# Revit family: WWF-Welded Wide Flange
name_source: partatom
category: Structural Framing
revit_build: Autodesk Revit Architecture 2012 (Build: 20110210_1515)
units: mm (PartAtom-declared; Revit-internal decimal feet)

## types (107) — shared parameters
Assembly Code = B10
Nominal d = 12

## per-type parameters (varying)
| type | A | W | bf | d | k | tf | tw |
| WWF79x490 | 144 in² | 490 | 1' - 9 5/8" | 6' - 6 3/4" | 0' - 0 13/16" | 0' - 2" | 0' - 0 13/16" |
| WWF79x436 | 128 in² | 436 | 1' - 9 5/8" | 6' - 6 3/4" | 0' - 0 13/16" | 0' - 1 9/16" | 0' - 0 13/16" |
| WWF79x408 | 120 in² | 408 | 1' - 9 5/8" | 6' - 6 3/4" | 0' - 0 13/16" | 0' - 1 3/8" | 0' - 0 13/16" |
| WWF79x364 | 107 in² | 364 | 1' - 7 11/16" | 6' - 6 3/4" | 0' - 0 13/16" | 0' - 1 3/16" | 0' - 0 13/16" |
| WWF71x470 | 138 in² | 470 | 1' - 9 5/8" | 5' - 10 7/8" | 0' - 0 13/16" | 0' - 2" | 0' - 0 13/16" |
| WWF71x442 | 130 in² | 442 | 1' - 9 5/8" | 5' - 10 7/8" | 0' - 0 13/16" | 0' - 1 3/4" | 0' - 0 13/16" |
| WWF71x415 | 122 in² | 415 | 1' - 9 5/8" | 5' - 10 7/8" | 0' - 0 13/16" | 0' - 1 9/16" | 0' - 0 13/16" |
| WWF71x388 | 114 in² | 388 | 1' - 9 5/8" | 5' - 10 7/8" | 0' - 0 13/16" | 0' - 1 3/8" | 0' - 0 13/16" |
| WWF71x344 | 101 in² | 344 | 1' - 7 11/16" | 5' - 10 7/8" | 0' - 0 13/16" | 0' - 1 3/16" | 0' - 0 13/16" |
| WWF63x419 | 123 in² | 419 | 1' - 9 5/8" | 5' - 3" | 0' - 0 3/4" | 0' - 2" | 0' - 0 5/8" |
| WWF63x388 | 114 in² | 388 | 1' - 9 5/8" | 5' - 3" | 0' - 0 3/4" | 0' - 1 3/4" | 0' - 0 5/8" |
| WWF63x361 | 106 in² | 361 | 1' - 9 5/8" | 5' - 3" | 0' - 0 3/4" | 0' - 1 9/16" | 0' - 0 5/8" |
| WWF63x333 | 97.8 in² | 333 | 1' - 9 5/8" | 5' - 3" | 0' - 0 11/16" | 0' - 1 3/8" | 0' - 0 5/8" |
| WWF63x289 | 84.9 in² | 289 | 1' - 7 11/16" | 5' - 3" | 0' - 0 11/16" | 0' - 1 3/16" | 0' - 0 5/8" |
| WWF55x402 | 118 in² | 402 | 1' - 9 5/8" | 4' - 7 1/8" | 0' - 0 3/4" | 0' - 2" | 0' - 0 5/8" |
| WWF55x344 | 101 in² | 344 | 1' - 9 5/8" | 4' - 7 1/8" | 0' - 0 3/4" | 0' - 1 9/16" | 0' - 0 5/8" |
| WWF55x316 | 92.9 in² | 316 | 1' - 9 5/8" | 4' - 7 1/8" | 0' - 0 11/16" | 0' - 1 3/8" | 0' - 0 5/8" |
| WWF55x272 | 79.9 in² | 272 | 1' - 7 11/16" | 4' - 7 1/8" | 0' - 0 11/16" | 0' - 1 3/16" | 0' - 0 5/8" |
| WWF55x240 | 70.6 in² | 240 | 1' - 3 3/4" | 4' - 7 1/8" | 0' - 0 11/16" | 0' - 1 3/16" | 0' - 0 5/8" |
| WWF47x326 | 96.3 in² | 326 | 1' - 9 5/8" | 3' - 11 1/4" | 0' - 0 3/4" | 0' - 1 9/16" | 0' - 0 5/8" |
| WWF47x281 | 82.5 in² | 281 | 1' - 7 11/16" | 3' - 11 1/4" | 0' - 0 11/16" | 0' - 1 3/8" | 0' - 0 5/8" |
| WWF47x255 | 75 in² | 255 | 1' - 7 11/16" | 3' - 11 1/4" | 0' - 0 11/16" | 0' - 1 3/16" | 0' - 0 5/8" |
| WWF47x224 | 65.7 in² | 224 | 1' - 3 3/4" | 3' - 11 1/4" | 0' - 0 11/16" | 0' - 1 3/16" | 0' - 0 5/8" |
| WWF47x203 | 59.7 in² | 203 | 1' - 3 3/4" | 3' - 11 1/4" | 0' - 0 11/16" | 0' - 1" | 0' - 0 5/8" |
| WWF47x176 | 52 in² | 176 | 0' - 11 13/16" | 3' - 11 1/4" | 0' - 0 11/16" | 0' - 1" | 0' - 0 5/8" |
| WWF43x307 | 90.6 in² | 307 | 1' - 9 5/8" | 3' - 7 5/16" | 0' - 0 11/16" | 0' - 1 9/16" | 0' - 0 9/16" |
| WWF43x260 | 76.8 in² | 260 | 1' - 7 11/16" | 3' - 7 5/16" | 0' - 0 5/8" | 0' - 1 3/8" | 0' - 0 9/16" |
| WWF43x236 | 69.3 in² | 236 | 1' - 7 11/16" | 3' - 7 5/16" | 0' - 0 5/8" | 0' - 1 3/16" | 0' - 0 9/16" |
| WWF43x204 | 60 in² | 204 | 1' - 3 3/4" | 3' - 7 5/16" | 0' - 0 5/8" | 0' - 1 3/16" | 0' - 0 9/16" |
| WWF43x184 | 54 in² | 184 | 1' - 3 3/4" | 3' - 7 5/16" | 0' - 0 5/8" | 0' - 1" | 0' - 0 9/16" |
| WWF43x157 | 46.2 in² | 157 | 0' - 11 13/16" | 3' - 7 5/16" | 0' - 0 5/8" | 0' - 1" | 0' - 0 9/16" |
| WWF39x300 | 88.4 in² | 300 | 1' - 9 5/8" | 3' - 3 3/8" | 0' - 0 11/16" | 0' - 1 9/16" | 0' - 0 9/16" |
| WWF39x253 | 74.6 in² | 253 | 1' - 7 11/16" | 3' - 3 3/8" | 0' - 0 5/8" | 0' - 1 3/8" | 0' - 0 9/16" |
| WWF39x228 | 67.1 in² | 228 | 1' - 7 11/16" | 3' - 3 3/8" | 0' - 0 5/8" | 0' - 1 3/16" | 0' - 0 9/16" |
| WWF39x197 | 57.8 in² | 197 | 1' - 3 3/4" | 3' - 3 3/8" | 0' - 0 5/8" | 0' - 1 3/16" | 0' - 0 9/16" |
| WWF39x176 | 51.8 in² | 176 | 1' - 3 3/4" | 3' - 3 3/8" | 0' - 0 5/8" | 0' - 1" | 0' - 0 9/16" |
| WWF39x150 | 44.1 in² | 150 | 0' - 11 13/16" | 3' - 3 3/8" | 0' - 0 5/8" | 0' - 1" | 0' - 0 9/16" |
| WWF39x134 | 39.6 in² | 134 | 0' - 11 13/16" | 3' - 3 3/8" | 0' - 0 5/8" | 0' - 0 13/16" | 0' - 0 9/16" |
| WWF35x279 | 82.5 in² | 279 | 1' - 9 5/8" | 2' - 11 7/16" | 0' - 0 5/8" | 0' - 1 9/16" | 0' - 0 7/16" |
| WWF35x233 | 68.6 in² | 233 | 1' - 7 11/16" | 2' - 11 7/16" | 0' - 0 9/16" | 0' - 1 3/8" | 0' - 0 7/16" |
| WWF35x208 | 61 in² | 208 | 1' - 7 11/16" | 2' - 11 7/16" | 0' - 0 9/16" | 0' - 1 3/16" | 0' - 0 7/16" |
| WWF35x176 | 51.7 in² | 176 | 1' - 3 3/4" | 2' - 11 7/16" | 0' - 0 9/16" | 0' - 1 3/16" | 0' - 0 7/16" |
| WWF35x156 | 45.7 in² | 156 | 1' - 3 3/4" | 2' - 11 7/16" | 0' - 0 9/16" | 0' - 1" | 0' - 0 7/16" |
| WWF35x128 | 37.9 in² | 128 | 0' - 11 13/16" | 2' - 11 7/16" | 0' - 0 9/16" | 0' - 1" | 0' - 0 7/16" |
| WWF35x113 | 33.5 in² | 113 | 0' - 11 13/16" | 2' - 11 7/16" | 0' - 0 9/16" | 0' - 0 13/16" | 0' - 0 7/16" |
| WWF31x228 | 66.9 in² | 228 | 1' - 7 11/16" | 2' - 7 1/2" | 0' - 0 9/16" | 0' - 1 3/8" | 0' - 0 7/16" |
| WWF31x202 | 59.3 in² | 202 | 1' - 7 11/16" | 2' - 7 1/2" | 0' - 0 9/16" | 0' - 1 3/16" | 0' - 0 7/16" |
| WWF31x170 | 50 in² | 170 | 1' - 3 3/4" | 2' - 7 1/2" | 0' - 0 9/16" | 0' - 1 3/16" | 0' - 0 7/16" |
| WWF31x150 | 44 in² | 150 | 1' - 3 3/4" | 2' - 7 1/2" | 0' - 0 9/16" | 0' - 1" | 0' - 0 7/16" |
| WWF31x123 | 36.2 in² | 123 | 0' - 11 13/16" | 2' - 7 1/2" | 0' - 0 9/16" | 0' - 1" | 0' - 0 7/16" |
| WWF31x108 | 31.8 in² | 108 | 0' - 11 13/16" | 2' - 7 1/2" | 0' - 0 9/16" | 0' - 0 13/16" | 0' - 0 7/16" |
| WWF28x164 | 48.3 in² | 164 | 1' - 3 3/4" | 2' - 3 9/16" | 0' - 0 9/16" | 0' - 1 3/16" | 0' - 0 7/16" |
| WWF28x144 | 42.3 in² | 144 | 1' - 3 3/4" | 2' - 3 9/16" | 0' - 0 9/16" | 0' - 1" | 0' - 0 7/16" |
| WWF28x132 | 38.7 in² | 132 | 1' - 3 3/4" | 2' - 3 9/16" | 0' - 0 9/16" | 0' - 0 7/8" | 0' - 0 7/16" |
| WWF28x117 | 34.5 in² | 117 | 0' - 11 13/16" | 2' - 3 9/16" | 0' - 0 9/16" | 0' - 1" | 0' - 0 7/16" |
| WWF28x102 | 30 in² | 102 | 0' - 11 13/16" | 2' - 3 9/16" | 0' - 0 9/16" | 0' - 0 13/16" | 0' - 0 7/16" |
| WWF26x580 | 170 in² | 580 | 2' - 1 9/16" | 2' - 1 9/16" | 0' - 1 5/8" | 0' - 2 3/8" | 0' - 2 3/8" |
| WWF26x497 | 146 in² | 497 | 2' - 1 9/16" | 2' - 1 9/16" | 0' - 1" | 0' - 2 3/8" | 0' - 1 3/16" |
| WWF26x402 | 118 in² | 402 | 2' - 1 9/16" | 2' - 1 9/16" | 0' - 0 13/16" | 0' - 2" | 0' - 0 13/16" |
| WWF26x336 | 98.5 in² | 336 | 2' - 1 9/16" | 2' - 1 9/16" | 0' - 0 13/16" | 0' - 1 9/16" | 0' - 0 13/16" |
| WWF26x269 | 79 in² | 269 | 2' - 1 9/16" | 2' - 1 9/16" | 0' - 0 13/16" | 0' - 1 3/16" | 0' - 0 13/16" |
| WWF24x531 | 157 in² | 531 | 1' - 11 5/8" | 1' - 11 5/8" | 0' - 1 5/8" | 0' - 2 3/8" | 0' - 2 3/8" |
| WWF24x456 | 134 in² | 456 | 1' - 11 5/8" | 1' - 11 5/8" | 0' - 1" | 0' - 2 3/8" | 0' - 1 3/16" |
| WWF24x371 | 109 in² | 371 | 1' - 11 5/8" | 1' - 11 5/8" | 0' - 0 13/16" | 0' - 2" | 0' - 0 13/16" |
| WWF24x309 | 90.8 in² | 309 | 1' - 11 5/8" | 1' - 11 5/8" | 0' - 0 13/16" | 0' - 1 9/16" | 0' - 0 13/16" |
| WWF24x248 | 72.8 in² | 248 | 1' - 11 5/8" | 1' - 11 5/8" | 0' - 0 13/16" | 0' - 1 3/16" | 0' - 0 13/16" |
| WWF22x484 | 143 in² | 484 | 1' - 9 5/8" | 1' - 9 5/8" | 0' - 1 7/8" | 0' - 2 3/8" | 0' - 2 3/8" |
| WWF22x416 | 123 in² | 416 | 1' - 9 5/8" | 1' - 9 5/8" | 0' - 1" | 0' - 2 3/8" | 0' - 1 3/16" |
| WWF22x338 | 99.5 in² | 338 | 1' - 9 5/8" | 1' - 9 5/8" | 0' - 0 13/16" | 0' - 2" | 0' - 0 13/16" |
| WWF22x282 | 83 in² | 282 | 1' - 9 5/8" | 1' - 9 5/8" | 0' - 0 13/16" | 0' - 1 9/16" | 0' - 0 13/16" |
| WWF22x188 | 55.2 in² | 188 | 1' - 9 5/8" | 1' - 9 5/8" | 0' - 0 11/16" | 0' - 1" | 0' - 0 5/8" |
| WWF20x437 | 129 in² | 437 | 1' - 7 11/16" | 1' - 7 11/16" | 0' - 1 7/8" | 0' - 2 3/8" | 0' - 2 3/8" |
| WWF20x377 | 111 in² | 377 | 1' - 7 11/16" | 1' - 7 11/16" | 0' - 1" | 0' - 2 3/8" | 0' - 1 3/16" |
| WWF20x306 | 90.2 in² | 306 | 1' - 7 11/16" | 1' - 7 11/16" | 0' - 0 13/16" | 0' - 2" | 0' - 0 13/16" |
| WWF20x256 | 75.3 in² | 256 | 1' - 7 11/16" | 1' - 7 11/16" | 0' - 0 13/16" | 0' - 1 9/16" | 0' - 0 13/16" |
| WWF20x230 | 67.9 in² | 230 | 1' - 7 11/16" | 1' - 7 11/16" | 0' - 0 13/16" | 0' - 1 3/8" | 0' - 0 13/16" |
| WWF20x205 | 60.4 in² | 205 | 1' - 7 11/16" | 1' - 7 11/16" | 0' - 0 13/16" | 0' - 1 3/16" | 0' - 0 13/16" |
| WWF20x185 | 54.6 in² | 185 | 1' - 7 11/16" | 1' - 7 11/16" | 0' - 0 13/16" | 0' - 1 1/8" | 0' - 0 5/8" |
| WWF20x170 | 50.1 in² | 170 | 1' - 7 11/16" | 1' - 7 11/16" | 0' - 0 13/16" | 0' - 1" | 0' - 0 5/8" |
| WWF20x150 | 44.2 in² | 150 | 1' - 7 11/16" | 1' - 7 11/16" | 0' - 0 5/8" | 0' - 0 7/8" | 0' - 0 9/16" |
| WWF20x132 | 39 in² | 132 | 1' - 7 11/16" | 1' - 7 11/16" | 0' - 0 9/16" | 0' - 0 13/16" | 0' - 0 7/16" |
| WWF18x337 | 99.3 in² | 337 | 1' - 5 3/4" | 1' - 5 3/4" | 0' - 1" | 0' - 2 3/8" | 0' - 1 3/16" |
| WWF18x275 | 80.9 in² | 275 | 1' - 5 3/4" | 1' - 5 3/4" | 0' - 0 13/16" | 0' - 2" | 0' - 0 13/16" |
| WWF18x229 | 67.5 in² | 229 | 1' - 5 3/4" | 1' - 5 3/4" | 0' - 0 13/16" | 0' - 1 9/16" | 0' - 0 13/16" |
| WWF18x207 | 60.9 in² | 207 | 1' - 5 3/4" | 1' - 5 3/4" | 0' - 0 13/16" | 0' - 1 3/8" | 0' - 0 13/16" |
| WWF18x184 | 54.2 in² | 184 | 1' - 5 3/4" | 1' - 5 3/4" | 0' - 0 13/16" | 0' - 1 3/16" | 0' - 0 13/16" |
| WWF18x166 | 49 in² | 166 | 1' - 5 3/4" | 1' - 5 3/4" | 0' - 0 11/16" | 0' - 1 1/8" | 0' - 0 5/8" |
| WWF18x152 | 45 in² | 152 | 1' - 5 3/4" | 1' - 5 3/4" | 0' - 0 11/16" | 0' - 1" | 0' - 0 5/8" |
| WWF18x134 | 39.7 in² | 134 | 1' - 5 3/4" | 1' - 5 3/4" | 0' - 0 5/8" | 0' - 0 7/8" | 0' - 0 9/16" |
| WWF18x119 | 35.1 in² | 119 | 1' - 5 3/4" | 1' - 5 3/4" | 0' - 0 9/16" | 0' - 0 13/16" | 0' - 0 7/16" |
| WWF16x298 | 87.7 in² | 298 | 1' - 3 3/4" | 1' - 3 3/4" | 0' - 1" | 0' - 2 3/8" | 0' - 1 3/16" |
| WWF16x243 | 71.6 in² | 243 | 1' - 3 3/4" | 1' - 3 3/4" | 0' - 0 13/16" | 0' - 2" | 0' - 0 13/16" |
| WWF16x203 | 59.8 in² | 203 | 1' - 3 3/4" | 1' - 3 3/4" | 0' - 0 13/16" | 0' - 1 9/16" | 0' - 0 13/16" |
| WWF16x183 | 53.9 in² | 183 | 1' - 3 3/4" | 1' - 3 3/4" | 0' - 0 13/16" | 0' - 1 3/8" | 0' - 0 13/16" |
| WWF16x163 | 48 in² | 163 | 1' - 3 3/4" | 1' - 3 3/4" | 0' - 0 13/16" | 0' - 1 3/16" | 0' - 0 13/16" |
| WWF16x147 | 43.4 in² | 147 | 1' - 3 3/4" | 1' - 3 3/4" | 0' - 0 11/16" | 0' - 1 1/8" | 0' - 0 5/8" |
| WWF16x135 | 39.9 in² | 135 | 1' - 3 3/4" | 1' - 3 3/4" | 0' - 0 11/16" | 0' - 1" | 0' - 0 5/8" |
| WWF16x119 | 35.2 in² | 119 | 1' - 3 3/4" | 1' - 3 3/4" | 0' - 0 5/8" | 0' - 0 7/8" | 0' - 0 9/16" |
| WWF16x105 | 31.1 in² | 105 | 1' - 3 3/4" | 1' - 3 3/4" | 0' - 0 9/16" | 0' - 0 13/16" | 0' - 0 7/16" |
| WWF14x211 | 62.3 in² | 211 | 1' - 1 3/4" | 1' - 1 3/4" | 0' - 0 13/16" | 0' - 2" | 0' - 0 13/16" |
| WWF14x177 | 52 in² | 177 | 1' - 1 3/4" | 1' - 1 3/4" | 0' - 0 13/16" | 0' - 1 9/16" | 0' - 0 13/16" |
| WWF14x159 | 46.9 in² | 159 | 1' - 1 3/4" | 1' - 1 3/4" | 0' - 0 13/16" | 0' - 1 3/8" | 0' - 0 13/16" |
| WWF14x142 | 41.8 in² | 142 | 1' - 1 3/4" | 1' - 1 3/4" | 0' - 0 13/16" | 0' - 1 3/16" | 0' - 0 13/16" |
| WWF14x128 | 37.9 in² | 128 | 1' - 1 3/4" | 1' - 1 3/4" | 0' - 0 13/16" | 0' - 1 1/8" | 0' - 0 5/8" |
| WWF14x118 | 34.8 in² | 118 | 1' - 1 3/4" | 1' - 1 3/4" | 0' - 0 13/16" | 0' - 1" | 0' - 0 5/8" |
| WWF14x104 | 30.7 in² | 104 | 1' - 1 3/4" | 1' - 1 3/4" | 0' - 0 5/8" | 0' - 0 7/8" | 0' - 0 9/16" |
| WWF14x92 | 27.2 in² | 92 | 1' - 1 3/4" | 1' - 1 3/4" | 0' - 0 9/16" | 0' - 0 13/16" | 0' - 0 7/16" |

## geometry (parser evidence)
native form markers: Sweep x2
no freeform markers — native parametric forms only
